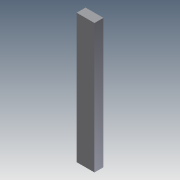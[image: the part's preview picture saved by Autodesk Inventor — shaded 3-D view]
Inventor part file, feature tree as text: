
AUTODESK INVENTOR PART (.ipt)
format: ipt  version: 2011 (Build 150239000, 239)  size: 657,920 bytes
history: native  units: in
note: dims shown in document units (in); Inventor stores cm internally (conversion verified against a paired STEP export)
features: extrude x31, sketch x31
ambient origin geometry x8: Origin, YZ Plane, XZ Plane, XY Plane, X Axis, Y Axis, Z Axis, Center Point
bodies: Solid1 (feature_tree)
feature tree (62):
  extrude  "Extrusion1"  Depth=6.75in
  extrude  "Extrusion2"  Depth=0.5in
  extrude  "Extrusion3"  Depth=0.5in
  extrude  "Extrusion4"  Depth=5.75in
  extrude  "Extrusion5"  Depth=0.5in
  extrude  "Extrusion6"  Depth=1.5in
  extrude  "Extrusion7"  Depth=1.5in
  extrude  "Extrusion8"  Depth=0.156in
  extrude  "Extrusion9"  Depth=0.25in TaperAngle=0.0deg
  extrude  "Extrusion10"  Depth=0.25in TaperAngle=0.0deg
  extrude  "Extrusion11"  Depth=0.25in TaperAngle=0.0deg
  extrude  "Extrusion12"  Depth=0.25in
  extrude  "Extrusion13"  Depth=0.25in
  extrude  "Extrusion14"  Depth=0.25in TaperAngle=0.0deg
  extrude  "Extrusion15"  Depth=3.0in
  extrude  "Extrusion16"  Depth=0.25in TaperAngle=0.0deg
  extrude  "Extrusion17"  Depth=1.0in
  extrude  "Extrusion18"  Depth=0.25in TaperAngle=0.0deg
  extrude  "Extrusion19"  Depth=0.25in TaperAngle=0.0deg
  extrude  "Extrusion20"  Depth=0.25in TaperAngle=0.0deg
  extrude  "Extrusion21"  Depth=1.0in
  extrude  "Extrusion22"  Depth=1.0in
  extrude  "Extrusion23"  Depth=2.0in
  extrude  "Extrusion24"  Depth=0.5in
  extrude  "Extrusion25"  Depth=0.5in
  extrude  "Extrusion26"  Depth=0.5in
  extrude  "Extrusion27"  Depth=0.5in
  extrude  "Extrusion28"  Depth=0.5in
  extrude  "Extrusion29"  Depth=0.5in
  extrude  "Extrusion30"  Depth=0.25in TaperAngle=0.0deg
  extrude  "Extrusion31"  Depth=1.0in
  sketch  "Sketch1"  dims[d0=5.2in d1=6.75in]
  sketch  "Sketch2"  dims[d2=0.25in d3=0.5in]
  sketch  "Sketch3"  dims[d4=5.7in d5=0.5in]
  sketch  "Sketch4"  dims[d6=0.5in d7=5.75in]
  sketch  "Sketch5"  dims[d8=0.375in d9=0.5in]
  sketch  "Sketch6"  dims[d10=0.25in d11=1.5in]
  sketch  "Sketch7"  dims[d12=0.25in d13=1.5in]
  sketch  "Sketch8"  dims[d14=0.25in d15=0.156in]
  sketch  "Sketch9"  dims[d16=0.156in d17=0.25in d18=0.0in]
  sketch  "Sketch10"  dims[d19=0.125in d20=0.0in d21=0.25in d22=0.0in]
  sketch  "Sketch11"  dims[d23=0.25in d24=0.0in d25=0.25in d26=0.0in]
  sketch  "Sketch12"  dims[d27=0.25in d28=0.25in]
  sketch  "Sketch13"  dims[d29=0.25in d30=0.25in]
  sketch  "Sketch14"  dims[d31=0.25in d32=0.25in d33=0.0in]
  sketch  "Sketch15"  dims[d34=1.5in d35=3.0in]
  sketch  "Sketch16"  dims[d36=1.0in d37=0.25in d38=0.0in]
  sketch  "Sketch17"  dims[d39=6.65in d40=1.0in]
  sketch  "Sketch18"  dims[d41=1.5in d42=0.25in d43=0.0in]
  sketch  "Sketch19"  dims[d44=0.25in d45=0.0in d46=0.25in d47=0.0in]
  sketch  "Sketch20"  dims[d48=1.0in d49=0.25in d50=0.0in]
  sketch  "Sketch21"  dims[d51=0.25in d52=1.0in]
  sketch  "Sketch22"  dims[d53=0.25in d54=1.0in]
  sketch  "Sketch23"  dims[d55=0.25in d56=2.0in]
  sketch  "Sketch24"  dims[d57=1.0in d58=0.5in]
  sketch  "Sketch25"  dims[d59=1.0in d60=0.5in]
  sketch  "Sketch26"  dims[d61=1.0in d62=0.5in]
  sketch  "Sketch27"  dims[d63=1.0in d64=0.5in]
  sketch  "Sketch28"  dims[d65=1.0in d66=0.5in]
  sketch  "Sketch29"  dims[d67=1.0in d68=0.5in]
  sketch  "Sketch30"  dims[d69=1.0in d70=0.25in d71=0.0in]
  sketch  "Sketch31"  dims[d72=0.25in d73=1.0in d74=1.0in d75=0.25in d76=0.0in d77=0.25in d78=0.0in d79=0.25in d80=0.25in d81=0.0in d82=0.75in d83=0.156in d84=0.156in d85=0.25in d86=0.0in d87=0.25in d88=0.0in d89=1.0in d90=1.0in d91=1.0in d92=0.25in d93=0.0in d94=1.0in d95=0.0in d96=1.0in d97=0.0in d98=1.0in d99=0.0in d100=0.5in d101=0.0in d102=0.5in d103=0.0in d104=0.25in d105=0.5in d106=0.0in d107=0.5in d108=0.0in d109=0.25in d110=0.0in d111=0.25in d112=0.0in d113=0.25in d114=0.5in d115=0.0in d116=0.25in d117=0.0in d118=0.5in d119=0.0in d120=0.5in d121=0.0in]
